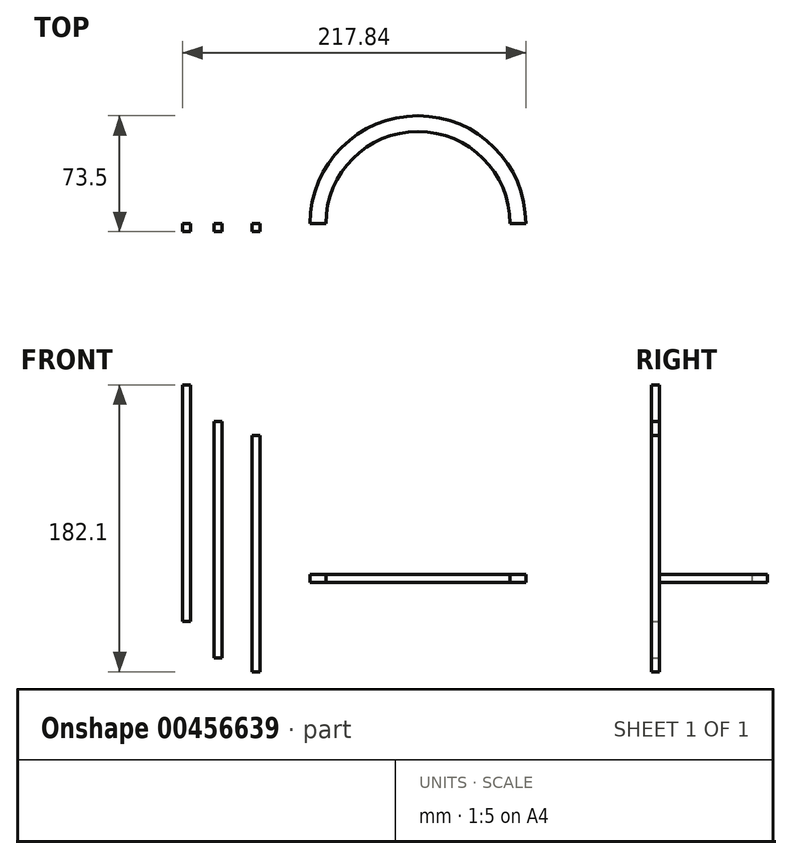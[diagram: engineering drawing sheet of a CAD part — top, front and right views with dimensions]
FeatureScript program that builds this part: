
annotation { "Feature Type Name" : "Feature", "Feature Type Description" : "" }
export const myFeature = defineFeature(function(context is Context, id is Id, definition is map)
    precondition{}
    {
        {
            var Q0;
            Q0=qCreatedBy(makeId("Top.planeOp"),FACE);
            var sketch = newSketch(context, id + "F0", { "sketchPlane" : qUnion([Q0])});
            skArc(sketch, "E0", {"start": v(-58.5, 0) * mm, "mid": v(0, 58.5) * mm, "end": v(58.5, 0) * mm});
            skPoint(sketch, "E1", {"position": v(0, 55.5) * mm});
            skArc(sketch, "E2.0", {"start": v(-68.5, 0) * mm, "mid": v(0, 68.5) * mm, "end": v(68.5, 0) * mm});
            skLineSegment(sketch, "E3", {"start": v(-68.5, 0) * mm, "end": v(-58.5, 0) * mm});
            skLineSegment(sketch, "E4", {"start": v(58.5, 0) * mm, "end": v(68.5, 0) * mm});
            skSolve(sketch);
        }
        {
            var Q0;
            Q0 = qSketchRegion(id + "F0", true);
            extrude(context, id + "F1", {"entities" : qUnion([Q0]), "depth" : 5 * mm});
        }
        {
            var Q0;
            Q0=qCreatedBy(makeId("Front.planeOp"),FACE);
            var sketch = newSketch(context, id + "F2", { "sketchPlane" : qUnion([Q0])});
            skLineSegment(sketch, "E5.bottom", {"start": v(-105.4, 93.16) * mm, "end": v(-100.4, 93.16) * mm});
            skLineSegment(sketch, "E5.top", {"start": v(-105.4, -56.84) * mm, "end": v(-100.4, -56.84) * mm});
            skLineSegment(sketch, "E5.left", {"start": v(-105.4, 93.16) * mm, "end": v(-105.4, -56.84) * mm});
            skLineSegment(sketch, "E5.right", {"start": v(-100.4, 93.16) * mm, "end": v(-100.4, -56.84) * mm});
            skLineSegment(sketch, "E6.bottom", {"start": v(-129.5, 101.98) * mm, "end": v(-124.5, 101.98) * mm});
            skLineSegment(sketch, "E6.top", {"start": v(-129.5, -48.02) * mm, "end": v(-124.5, -48.02) * mm});
            skLineSegment(sketch, "E6.left", {"start": v(-129.5, 101.98) * mm, "end": v(-129.5, -48.02) * mm});
            skLineSegment(sketch, "E6.right", {"start": v(-124.5, 101.98) * mm, "end": v(-124.5, -48.02) * mm});
            skLineSegment(sketch, "E7.bottom", {"start": v(-149.34, 125.26) * mm, "end": v(-144.34, 125.26) * mm});
            skLineSegment(sketch, "E7.top", {"start": v(-149.34, -24.74) * mm, "end": v(-144.34, -24.74) * mm});
            skLineSegment(sketch, "E7.left", {"start": v(-149.34, 125.26) * mm, "end": v(-149.34, -24.74) * mm});
            skLineSegment(sketch, "E7.right", {"start": v(-144.34, 125.26) * mm, "end": v(-144.34, -24.74) * mm});
            skSolve(sketch);
        }
        {
            var Q0;
            Q0 = qSketchRegion(id + "F2", true);
            extrude(context, id + "F3", {"entities" : qUnion([Q0]), "depth" : 5 * mm});
        }
    });
